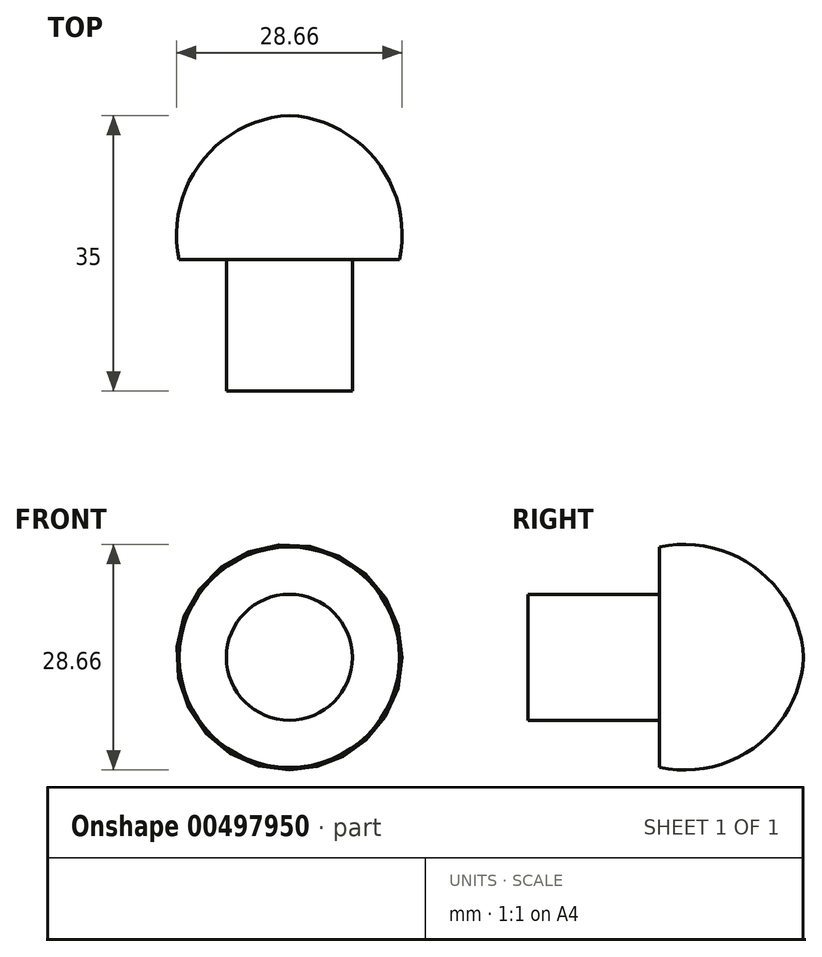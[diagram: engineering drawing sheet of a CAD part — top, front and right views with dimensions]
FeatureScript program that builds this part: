
annotation { "Feature Type Name" : "Feature", "Feature Type Description" : "" }
export const myFeature = defineFeature(function(context is Context, id is Id, definition is map)
    precondition{}
    {
        {
            var Q0;
            Q0=qCreatedBy(makeId("Top.planeOp"),FACE);
            var sketch = newSketch(context, id + "F0", { "sketchPlane" : qUnion([Q0])});
            skLineSegment(sketch, "E0", {"start": v(0, 0) * mm, "end": v(-8, 0) * mm});
            skLineSegment(sketch, "E1", {"start": v(-8, 0) * mm, "end": v(-8, 16.67) * mm});
            skLineSegment(sketch, "E2", {"start": v(-8, 16.67) * mm, "end": v(-14, 16.67) * mm});
            skArc(sketch, "E3", {"start": v(0, 35) * mm, "mid": v(-11.21, 29.05) * mm, "end": v(-14, 16.67) * mm});
            skLineSegment(sketch, "E4", {"start": v(0, 35) * mm, "end": v(0, 0) * mm});
            skSolve(sketch);
        }
        {
            var Q0;
            Q0=makeQuery(id+"F0.imprint","IMPRINT",FACE,{"disambiguationData":[TD([[makeQuery(id+"F0.imprint","IMPRINT",EDGE,{"derivedFrom":sQuery(id+"F0.wireOp",EDGE,"E0")}),-1.0]])]});
            var Q1;
            Q1=sQuery(id+"F0.wireOp",EDGE,"E4");
            revolve(context, id + "F1", {"entities" : qUnion([Q0]), "axis" : qUnion([Q1]), "revolveType" : RevolveType.FULL});
        }
    });
